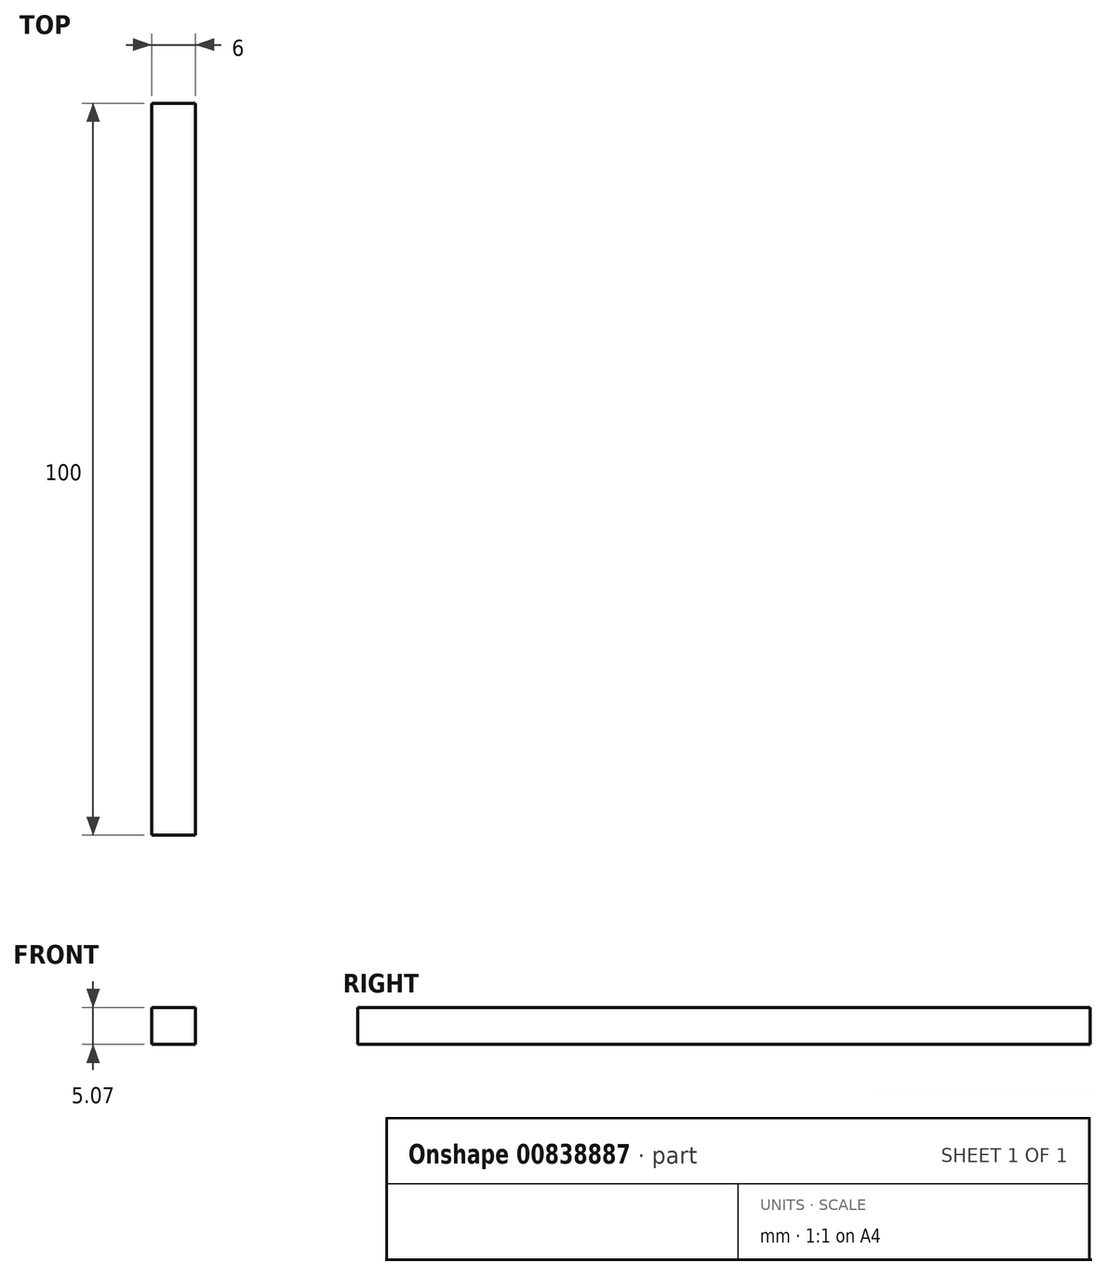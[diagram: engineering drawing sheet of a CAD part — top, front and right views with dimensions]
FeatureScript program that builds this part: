
annotation { "Feature Type Name" : "Feature", "Feature Type Description" : "" }
export const myFeature = defineFeature(function(context is Context, id is Id, definition is map)
    precondition{}
    {
        {
            var Q0;
            Q0=qCreatedBy(makeId("Front.planeOp"),FACE);
            var sketch = newSketch(context, id + "F0", { "sketchPlane" : qUnion([Q0])});
            skLineSegment(sketch, "E0.bottom", {"start": v(0, 63.83) * mm, "end": v(-6, 63.83) * mm});
            skLineSegment(sketch, "E0.top", {"start": v(0, 68.9) * mm, "end": v(-6, 68.9) * mm});
            skLineSegment(sketch, "E0.left", {"start": v(0, 63.83) * mm, "end": v(0, 68.9) * mm});
            skLineSegment(sketch, "E0.right", {"start": v(-6, 63.83) * mm, "end": v(-6, 68.9) * mm});
            skSolve(sketch);
        }
        {
            var Q0;
            Q0=makeQuery(id+"F0.imprint","IMPRINT",FACE,{"disambiguationData":[TD([[makeQuery(id+"F0.imprint","IMPRINT",EDGE,{"derivedFrom":sQuery(id+"F0.wireOp",EDGE,"E0.bottom")}),-1.0]])]});
            extrude(context, id + "F1", {"entities" : qUnion([Q0]), "depth" : 100 * mm, "offsetDistance" : 25.4 * mm});
        }
    });
